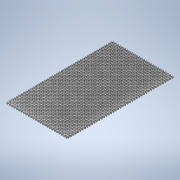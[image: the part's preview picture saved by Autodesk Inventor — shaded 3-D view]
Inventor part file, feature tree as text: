
AUTODESK INVENTOR PART (.ipt)
format: ipt  version: 2022 (Build 260153000, 153)  size: 2,004,992 bytes
history: native  units: mm
features: extrude x2, pattern_linear x2, plane x2, sketch x2
ambient origin geometry x8: Origin, YZ Plane, XZ Plane, XY Plane, X Axis, Y Axis, Z Axis, Center Point
bodies: 实体1 (feature_tree)
feature tree (8):
  extrude  "拉伸1"  Depth=2.0mm TaperAngle=0.0deg
  extrude  "拉伸2"  Depth=2.0mm TaperAngle=0.0deg
  pattern_linear  "矩形阵列1"  Count1=26 Spacing1=2.0mm
  pattern_linear  "矩形阵列2"  Count1=45 Spacing1=2.0mm
  plane  "工作平面1"
  plane  "工作平面2"
  sketch  "草图3"  dims[d16=1.0mm d17=2.0mm d18=0.0mm]
  sketch  "草图4"  dims[d19=1.0mm d20=2.0mm d21=0.0mm d22=260.0mm d24=2.0mm d25=450.0mm d27=2.0mm]
